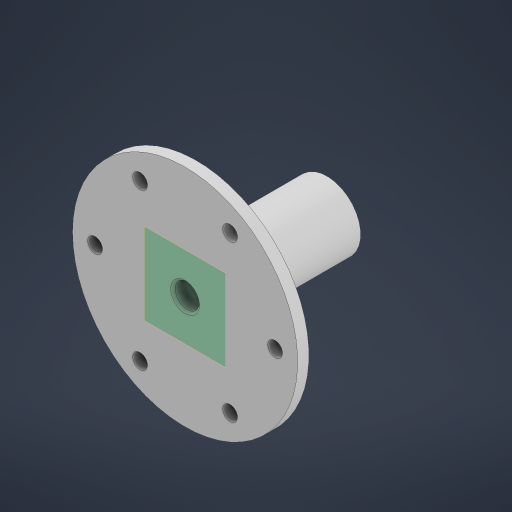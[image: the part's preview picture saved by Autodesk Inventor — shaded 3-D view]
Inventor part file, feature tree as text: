
AUTODESK INVENTOR PART (.ipt)
format: ipt  version: 2024.1 (Build 281209000, 209)  size: 241,152 bytes
history: native  units: in
note: dims shown in document units (in); Inventor stores cm internally (conversion verified against a paired STEP export)
features: extrude x6, other x5, sketch x4, reference x3, chamfer x2, plane x1
ambient origin geometry x8: Origin, YZ Plane, XZ Plane, XY Plane, X Axis, Y Axis, Z Axis, Center Point
bodies: Solid1 (feature_tree)
feature tree (21):
  extrude  "Extrusion1"  Depth=0.003in
  plane  "Work Plane1"
  sketch  "Sketch2"  dims[d2=0.5906in d3=2.2444in d4=0.0in d5=0.0in d6=5.4134in]
  extrude  "Extrusion2"  Depth=5.4134in
  extrude  "Extrusion3"  Depth=1.0in
  extrude  "Extrusion4"  Depth=0.125in
  extrude  "Extrusion5"  Depth=0.125in
  extrude  "Extrusion6"  Depth=1.0in
  chamfer  "Chamfer2"  Distance=2.3622in Angle=360.0deg
  chamfer  "Chamfer1"  Distance=1.0in
  sketch  "Sketch1"  dims[d0=0.002in d1=0.003in]
  reference  "Reference1"
  reference  "Reference2"
  sketch  "Sketch3"  dims[d7=21.6535in d8=1.0in]
  sketch  "Sketch4"  dims[d9=2.5in d10=24.0in d11=0.1654in d12=1.0in d13=2.3622in d15=360.0deg d17=1.0in d18=1.0in d19=0.75in d20=1.5748in d21=0.0in d22=0.4in d23=0.0in d24=0.125in d25=0.0in d26=0.35in d27=0.125in d28=45.0deg d29=1.2601in d30=0.0in d31=0.01in d32=1.5748in d33=0.0in d34=0.025in d35=0.125in d36=45.0deg]
  reference  "Reference3"
  other  "<userpath>\Documents\School\FallCAD\Trebuchet\Trebuchet.iam"
  other  "Trebuchet.iam"
  other  "BallBearing_8x22x7mm:1"
  other  "AcrylicRod:1"
  other  "Assembly1"
